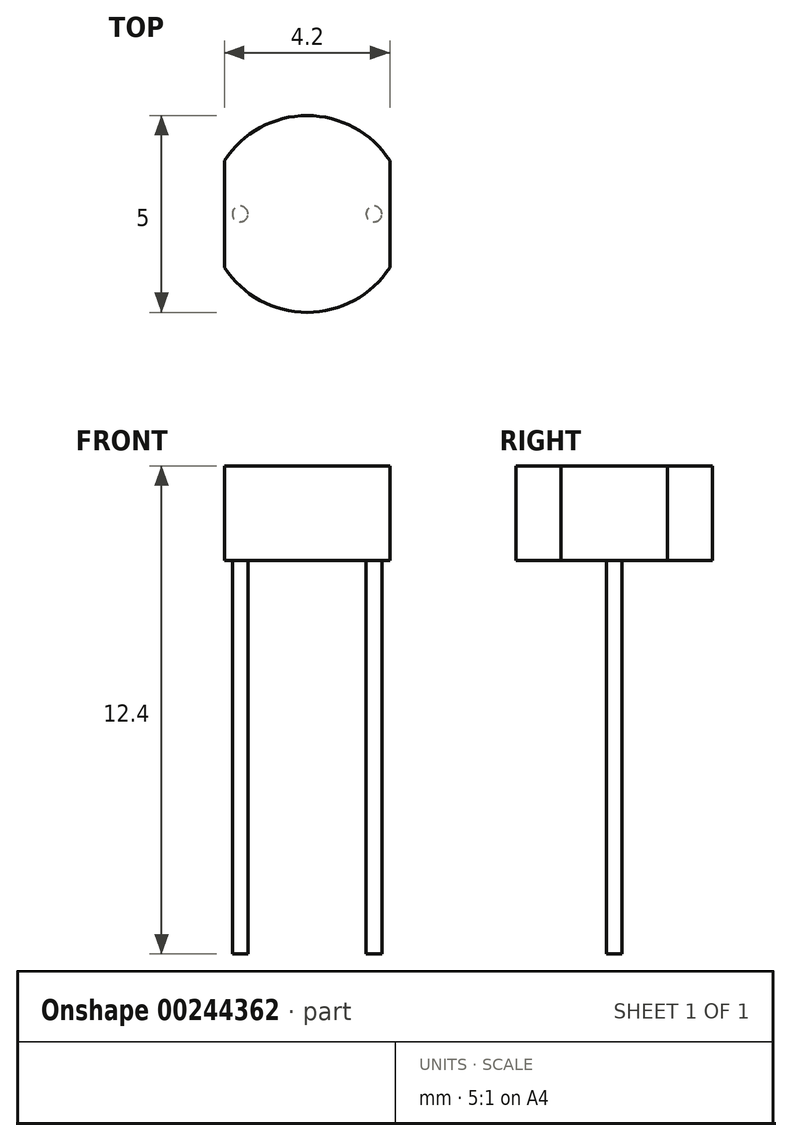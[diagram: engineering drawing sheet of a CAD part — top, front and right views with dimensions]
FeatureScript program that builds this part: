
annotation { "Feature Type Name" : "Feature", "Feature Type Description" : "" }
export const myFeature = defineFeature(function(context is Context, id is Id, definition is map)
    precondition{}
    {
        {
            var Q0;
            Q0=qCreatedBy(makeId("Top.planeOp"),FACE);
            var sketch = newSketch(context, id + "F0", { "sketchPlane" : qUnion([Q0])});
            skCircle(sketch, "E0", {"center": v(0, 0) * mm, "radius": 2.5 * mm});
            skSolve(sketch);
        }
        {
            var Q0;
            Q0 = qSketchRegion(id + "F0", true);
            extrude(context, id + "F1", {"entities" : qUnion([Q0]), "depth" : 2.4 * mm});
        }
        {
            var Q0;
            Q0=makeQuery(id+"F1.opExtrude","CAP_FACE",FACE,{"disambiguationData":[OSD([sQuery(id+"F0.wireOp",EDGE,"E0")])],"isStart":true});
            var sketch = newSketch(context, id + "F2", { "sketchPlane" : qUnion([Q0])});
            skCircle(sketch, "E1", {"center": v(-1.7, 0) * mm, "radius": 0.2 * mm});
            skCircle(sketch, "E2.MirrorC", {"center": v(1.7, 0) * mm, "radius": 0.2 * mm});
            skSolve(sketch);
        }
        {
            var Q0;
            Q0 = qSketchRegion(id + "F2", true);
            extrude(context, id + "F3", {"entities" : qUnion([Q0]), "depth" : 10 * mm});
        }
        {
            var Q0;
            Q0=makeQuery(id+"F1.opExtrude","CAP_FACE",FACE,{"disambiguationData":[OSD([sQuery(id+"F0.wireOp",EDGE,"E0")])],"isStart":false});
            var sketch = newSketch(context, id + "F4", { "sketchPlane" : qUnion([Q0])});
            skLineSegment(sketch, "E3.bottom", {"start": v(-2.1, 4.72) * mm, "end": v(2.1, 4.72) * mm});
            skLineSegment(sketch, "E3.top", {"start": v(-2.1, -5.8) * mm, "end": v(2.1, -5.8) * mm});
            skLineSegment(sketch, "E3.left", {"start": v(-2.1, 4.72) * mm, "end": v(-2.1, -5.8) * mm});
            skLineSegment(sketch, "E3.right", {"start": v(2.1, 4.72) * mm, "end": v(2.1, -5.8) * mm});
            skSolve(sketch);
        }
        {
            var Q0;
            Q0 = qSketchRegion(id + "F4", true);
            extrude(context, id + "F5", {"entities" : qUnion([Q0]), "operationType" : NewBodyOperationType.INTERSECT, "oppositeDirection" : true, "depth" : 25 * mm});
        }
    });
